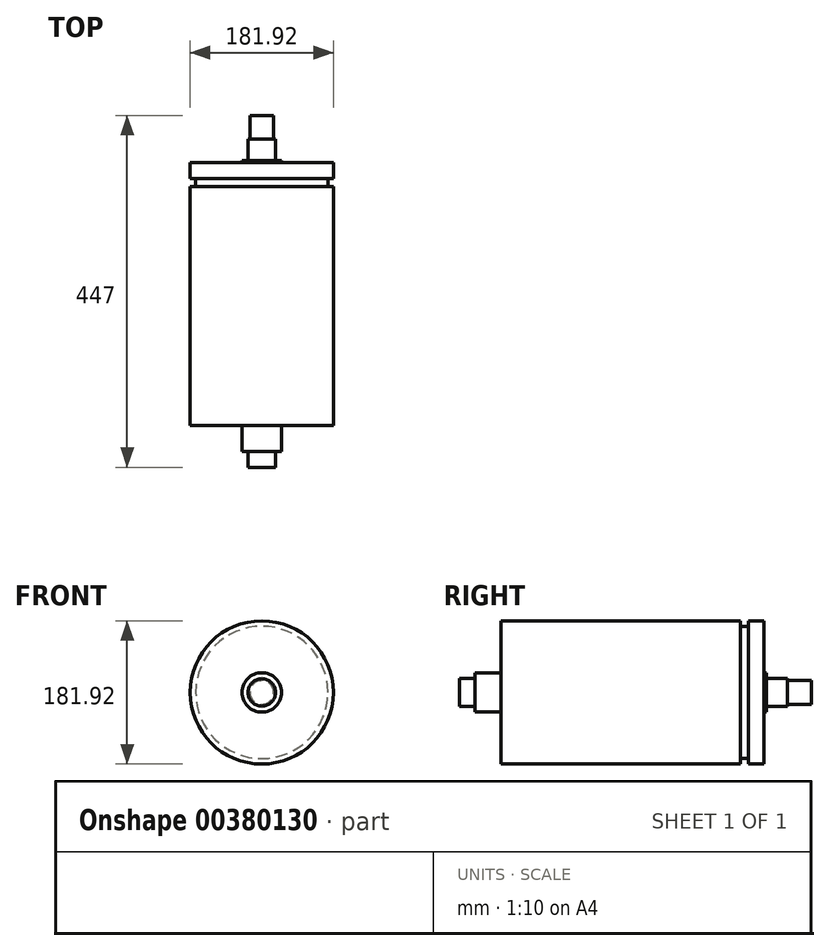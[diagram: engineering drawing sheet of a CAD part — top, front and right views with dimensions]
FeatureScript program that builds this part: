
annotation { "Feature Type Name" : "Feature", "Feature Type Description" : "" }
export const myFeature = defineFeature(function(context is Context, id is Id, definition is map)
    precondition{}
    {
        {
            var Q0;
            Q0=qCreatedBy(makeId("Front.planeOp"),FACE);
            var sketch = newSketch(context, id + "F0", { "sketchPlane" : qUnion([Q0])});
            skCircle(sketch, "E0", {"center": v(0, 0) * mm, "radius": 17.5 * mm});
            skSolve(sketch);
        }
        {
            var Q0;
            Q0=makeQuery(id+"F0.imprint","IMPRINT",FACE,{"disambiguationData":[TD([[makeQuery(id+"F0.imprint","IMPRINT",EDGE,{"derivedFrom":sQuery(id+"F0.wireOp",EDGE,"E0")}),1.0]])]});
            extrude(context, id + "F1", {"entities" : qUnion([Q0]), "oppositeDirection" : true, "depth" : 20 * mm});
        }
        {
            var Q0;
            Q0=makeQuery(id+"F1.opExtrude","CAP_FACE",FACE,{"disambiguationData":[OSD([sQuery(id+"F0.wireOp",EDGE,"E0")])],"isStart":false});
            var sketch = newSketch(context, id + "F2", { "sketchPlane" : qUnion([Q0])});
            skCircle(sketch, "E1", {"center": v(0, 0) * mm, "radius": 25 * mm});
            skSolve(sketch);
        }
        {
            var Q0;
            Q0=makeQuery(id+"F2.imprint","IMPRINT",FACE,{"disambiguationData":[TD([[makeQuery(id+"F2.imprint","IMPRINT",EDGE,{"derivedFrom":sQuery(id+"F2.wireOp",EDGE,"E1")}),1.0]])]});
            var Q1;
            Q1=makeQuery(id+"F2.imprint","IMPRINT",FACE,{"disambiguationData":[TD([[makeQuery(id+"F2.imprint","IMPRINT",EDGE,{"derivedFrom":makeQuery(id+"F1.opExtrude","CAP_EDGE",EDGE,{"disambiguationData":[OSD([sQuery(id+"F0.wireOp",EDGE,"E0")])],"isStart":false})}),-1.0]])]});
            extrude(context, id + "F3", {"entities" : qUnion([Q0, Q1]), "operationType" : NewBodyOperationType.ADD, "depth" : 33 * mm});
        }
        {
            var Q0;
            Q0=makeQuery(id+"F3.opExtrude","CAP_FACE",FACE,{"disambiguationData":[OSD([sQuery(id+"F2.wireOp",EDGE,"E1")])],"isStart":false});
            var sketch = newSketch(context, id + "F4", { "sketchPlane" : qUnion([Q0])});
            skCircle(sketch, "E2", {"center": v(0, 0) * mm, "radius": 90.96 * mm});
            skSolve(sketch);
        }
        {
            var Q0;
            Q0=makeQuery(id+"F4.imprint","IMPRINT",FACE,{"disambiguationData":[TD([[makeQuery(id+"F4.imprint","IMPRINT",EDGE,{"derivedFrom":sQuery(id+"F4.wireOp",EDGE,"E2")}),1.0]])]});
            var Q1;
            Q1=makeQuery(id+"F4.imprint","IMPRINT",FACE,{"disambiguationData":[TD([[makeQuery(id+"F4.imprint","IMPRINT",EDGE,{"derivedFrom":makeQuery(id+"F3.opExtrude","CAP_EDGE",EDGE,{"disambiguationData":[OSD([sQuery(id+"F2.wireOp",EDGE,"E1")])],"isStart":false})}),1.0]])]});
            extrude(context, id + "F5", {"entities" : qUnion([Q0, Q1]), "operationType" : NewBodyOperationType.ADD, "depth" : 304 * mm});
        }
        {
            var Q0;
            Q0=makeQuery(id+"F5.opExtrude","CAP_FACE",FACE,{"disambiguationData":[OSD([sQuery(id+"F4.wireOp",EDGE,"E2")])],"isStart":false});
            var sketch = newSketch(context, id + "F6", { "sketchPlane" : qUnion([Q0])});
            skCircle(sketch, "E3", {"center": v(0, 0) * mm, "radius": 84 * mm});
            skSolve(sketch);
        }
        {
            var Q0;
            Q0=makeQuery(id+"F6.imprint","IMPRINT",FACE,{"disambiguationData":[TD([[makeQuery(id+"F6.imprint","IMPRINT",EDGE,{"derivedFrom":sQuery(id+"F6.wireOp",EDGE,"E3")}),1.0]])]});
            extrude(context, id + "F7", {"entities" : qUnion([Q0]), "depth" : 10 * mm});
        }
        {
            var Q0;
            Q0=makeQuery(id+"F7.opExtrude","CAP_FACE",FACE,{"disambiguationData":[OSD([sQuery(id+"F6.wireOp",EDGE,"E3")])],"isStart":false});
            var sketch = newSketch(context, id + "F8", { "sketchPlane" : qUnion([Q0])});
            skCircle(sketch, "E4", {"center": v(0, 0) * mm, "radius": 90.96 * mm});
            skSolve(sketch);
        }
        {
            var Q0;
            Q0=makeQuery(id+"F8.imprint","IMPRINT",FACE,{"disambiguationData":[TD([[makeQuery(id+"F8.imprint","IMPRINT",EDGE,{"derivedFrom":sQuery(id+"F8.wireOp",EDGE,"E4")}),1.0]])]});
            var Q1;
            Q1=makeQuery(id+"F8.imprint","IMPRINT",FACE,{"disambiguationData":[TD([[makeQuery(id+"F8.imprint","IMPRINT",EDGE,{"derivedFrom":makeQuery(id+"F7.opExtrude","CAP_EDGE",EDGE,{"disambiguationData":[OSD([sQuery(id+"F6.wireOp",EDGE,"E3")])],"isStart":false})}),1.0]])]});
            extrude(context, id + "F9", {"entities" : qUnion([Q0, Q1]), "operationType" : NewBodyOperationType.ADD, "depth" : 20 * mm});
        }
        {
            var Q0;
            Q0=makeQuery(id+"F5.opExtrude","CAP_FACE",FACE,{"disambiguationData":[OSD([sQuery(id+"F4.wireOp",EDGE,"E2")])],"isStart":false});
            var sketch = newSketch(context, id + "F10", { "sketchPlane" : qUnion([Q0])});
            skCircle(sketch, "E5", {"center": v(0, 0) * mm, "radius": 25 * mm});
            skSolve(sketch);
        }
        {
            var Q0;
            Q0=makeQuery(id+"F10.imprint","IMPRINT",FACE,{"disambiguationData":[TD([[makeQuery(id+"F10.imprint","IMPRINT",EDGE,{"derivedFrom":sQuery(id+"F10.wireOp",EDGE,"E5")}),1.0]])]});
            extrude(context, id + "F11", {"entities" : qUnion([Q0]), "operationType" : NewBodyOperationType.ADD, "depth" : 33 * mm});
        }
        {
            var Q0;
            Q0=makeQuery(id+"F11.opExtrude","CAP_FACE",FACE,{"disambiguationData":[OSD([sQuery(id+"F10.wireOp",EDGE,"E5")])],"isStart":false});
            var sketch = newSketch(context, id + "F12", { "sketchPlane" : qUnion([Q0])});
            skCircle(sketch, "E6", {"center": v(0, 0) * mm, "radius": 17.5 * mm});
            skSolve(sketch);
        }
        {
            var Q0;
            Q0=makeQuery(id+"F12.imprint","IMPRINT",FACE,{"disambiguationData":[TD([[makeQuery(id+"F12.imprint","IMPRINT",EDGE,{"derivedFrom":sQuery(id+"F12.wireOp",EDGE,"E6")}),1.0]])]});
            var Q1;
            Q1=sQuery(id+"F12.wireOp",EDGE,"E6");
            extrude(context, id + "F13", {"entities" : qUnion([Q0]), "operationType" : NewBodyOperationType.ADD, "surfaceEntities" : qUnion([Q1]), "depth" : 27 * mm});
        }
        {
            var Q0;
            Q0=makeQuery(id+"F13.opExtrude","CAP_FACE",FACE,{"disambiguationData":[OSD([sQuery(id+"F12.wireOp",EDGE,"E6")])],"isStart":false});
            var sketch = newSketch(context, id + "F14", { "sketchPlane" : qUnion([Q0])});
            skCircle(sketch, "E7", {"center": v(0, 0) * mm, "radius": 15 * mm});
            skSolve(sketch);
        }
        {
            var Q0;
            Q0=makeQuery(id+"F14.imprint","IMPRINT",FACE,{"disambiguationData":[TD([[makeQuery(id+"F14.imprint","IMPRINT",EDGE,{"derivedFrom":sQuery(id+"F14.wireOp",EDGE,"E7")}),1.0]])]});
            extrude(context, id + "F15", {"entities" : qUnion([Q0]), "operationType" : NewBodyOperationType.ADD, "depth" : 30 * mm});
        }
    });
